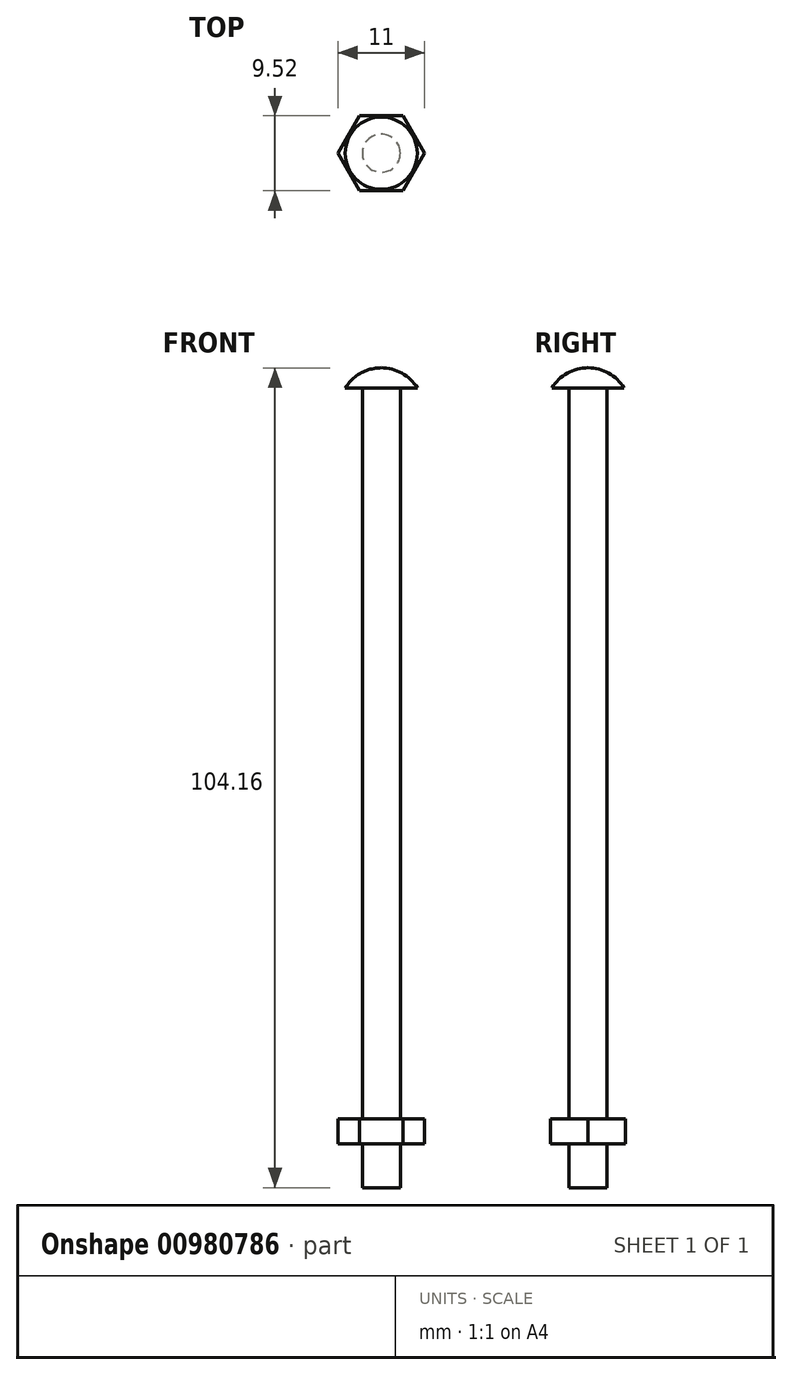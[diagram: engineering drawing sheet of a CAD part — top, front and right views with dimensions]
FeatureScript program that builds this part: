
annotation { "Feature Type Name" : "Feature", "Feature Type Description" : "" }
export const myFeature = defineFeature(function(context is Context, id is Id, definition is map)
    precondition{}
    {
        {
            var Q0;
            Q0=qCreatedBy(makeId("Front.planeOp"),FACE);
            var sketch = newSketch(context, id + "F0", { "sketchPlane" : qUnion([Q0])});
            skLineSegment(sketch, "E0", {"start": v(0, 92.87) * mm, "end": v(0, 0) * mm});
            skLineSegment(sketch, "E1", {"start": v(0, 0) * mm, "end": v(-2.41, 0) * mm});
            skLineSegment(sketch, "E2", {"start": v(-2.41, 0) * mm, "end": v(-2.41, 92.87) * mm});
            skLineSegment(sketch, "E3", {"start": v(-2.41, 92.87) * mm, "end": v(-4.58, 92.87) * mm});
            skArc(sketch, "E4", {"start": v(0, 95.43) * mm, "mid": v(-2.63, 94.75) * mm, "end": v(-4.58, 92.87) * mm});
            skLineSegment(sketch, "E5", {"start": v(0, 95.43) * mm, "end": v(4.27, 95.43) * mm, "construction": true});
            skLineSegment(sketch, "E6", {"start": v(0, 95.43) * mm, "end": v(0, 92.87) * mm});
            skSolve(sketch);
        }
        {
            var Q0;
            Q0=qSketchRegion(id+"F0",true);
            var Q1;
            Q1=sQuery(id+"F0.wireOp",EDGE,"E0");
            revolve(context, id + "F1", {"surfaceOperationType" : NewSurfaceOperationType.NEW, "entities" : qUnion([Q0]), "axis" : qUnion([Q1]), "revolveType" : RevolveType.FULL});
        }
        {
            var Q0;
            Q0=makeQuery(id+"F1.opRevolve","SWEPT_FACE",FACE,{"disambiguationData":[OSD([sQuery(id+"F0.wireOp",EDGE,"E1")])]});
            var sketch = newSketch(context, id + "F2", { "sketchPlane" : qUnion([Q0])});
            skCircle(sketch, "E7.cCircle", {"center": v(0, 0) * mm, "radius": 4.76 * mm, "construction": true});
            skLineSegment(sketch, "E7.0", {"start": v(-2.75, 4.76) * mm, "end": v(2.75, 4.76) * mm});
            skLineSegment(sketch, "E7.1", {"start": v(2.75, 4.76) * mm, "end": v(5.5, 0) * mm});
            skLineSegment(sketch, "E7.2", {"start": v(5.5, 0) * mm, "end": v(2.75, -4.76) * mm});
            skLineSegment(sketch, "E7.3", {"start": v(2.75, -4.76) * mm, "end": v(-2.75, -4.76) * mm});
            skLineSegment(sketch, "E7.4", {"start": v(-2.75, -4.76) * mm, "end": v(-5.5, 0) * mm});
            skLineSegment(sketch, "E7.5", {"start": v(-5.5, 0) * mm, "end": v(-2.75, 4.76) * mm});
            skPoint(sketch, "E7.0.midPoint", {"position": v(0, 4.76) * mm});
            skSolve(sketch);
        }
        {
            var Q0;
            Q0=qSketchRegion(id+"F2",true);
            extrude(context, id + "F3", {"entities" : qUnion([Q0]), "operationType" : NewBodyOperationType.ADD, "depth" : 3.17 * mm, "offsetDistance" : 25.4 * mm});
        }
        {
            var Q0;
            Q0=makeQuery(id+"F3.opExtrude","CAP_FACE",FACE,{"disambiguationData":[OSD([sQuery(id+"F2.wireOp",EDGE,"E7.0"),sQuery(id+"F2.wireOp",EDGE,"E7.1"),sQuery(id+"F2.wireOp",EDGE,"E7.2"),sQuery(id+"F2.wireOp",EDGE,"E7.3"),sQuery(id+"F2.wireOp",EDGE,"E7.4"),sQuery(id+"F2.wireOp",EDGE,"E7.5")])],"isStart":false});
            var sketch = newSketch(context, id + "F4", { "sketchPlane" : qUnion([Q0])});
            skCircle(sketch, "E8", {"center": v(0, 0) * mm, "radius": 2.41 * mm});
            skSolve(sketch);
        }
        {
            var Q0;
            Q0 = qSketchRegion(id + "F4", true);
            extrude(context, id + "F5", {"entities" : qUnion([Q0]), "operationType" : NewBodyOperationType.ADD, "depth" : 5.56 * mm, "offsetDistance" : 25.4 * mm});
        }
    });
